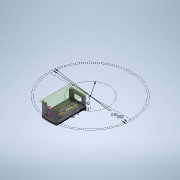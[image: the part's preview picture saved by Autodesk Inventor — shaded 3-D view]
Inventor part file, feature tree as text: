
AUTODESK INVENTOR PART (.ipt)
format: ipt  version: 2020 (Build 240168000, 168)  size: 668,160 bytes
history: native  units: mm
features: projected_geometry x30, extrude x16, sketch x11, fillet x10, other x6, chamfer x2
ambient origin geometry x8: Origin, YZ Plane, XZ Plane, XY Plane, X Axis, Y Axis, Z Axis, Center Point
bodies: Body1 (feature_tree)
feature tree (75):
  other  "Твердое тело1"
  sketch  "Эскиз1"
  extrude  "Выдавливание3"  Depth=202.0mm
  other  "РабПлоскость1"
  extrude  "Выдавливание1"  Depth=35.0mm
  other  "РабПлоскость2"
  sketch  "Эскиз2"
  extrude  "Выдавливание4"  Depth=68.0mm
  extrude  "Выдавливание5"  Depth=2.0mm
  sketch  "Эскиз4"
  extrude  "Выдавливание6"  Depth=2.0mm
  extrude  "Выдавливание7"  Depth=3.0mm
  other  "РабПлоскость3"
  extrude  "Выдавливание8"  Depth=3.0mm
  other  "РабПлоскость4"
  extrude  "Выдавливание9"  Depth=210.0mm
  sketch  "Эскиз8"
  extrude  "Выдавливание10"  Depth=20.0mm TaperAngle=0.0deg
  fillet  "Сопряжение1"  Radius=1.5mm
  fillet  "Сопряжение2"  Radius=28.0mm
  fillet  "Сопряжение3"  Radius=7.0mm
  fillet  "Сопряжение4"  Radius=20.0mm
  fillet  "Сопряжение5"  Radius=13.0mm
  extrude  "Выдавливание11"  Depth=5.0mm
  extrude  "Выдавливание12"  Depth=3.0mm
  fillet  "Сопряжение6"  Radius=10.0mm
  extrude  "Выдавливание13"  Depth=84.0mm
  chamfer  "Фаска1"  Distance=5.0mm
  fillet  "Сопряжение7"  Radius=52.0mm
  sketch  "Эскиз10"
  other  "РабПлоскость5"
  extrude  "Выдавливание14"  Depth=5.0mm TaperAngle=0.0deg
  fillet  "Сопряжение8"  Radius=35.0mm
  extrude  "Выдавливание15"  Depth=18.0mm
  fillet  "Сопряжение9"  Radius=3.0mm
  extrude  "Выдавливание16"  Depth=30.0mm TaperAngle=360.0deg
  fillet  "Сопряжение10"  Radius=0.5mm
  extrude  "Выдавливание17"  TaperAngle=0.0deg  [1 undecoded]
  chamfer  "Фаска2"  Distance=8.0mm
  projected_geometry  "Спроецированная петля1"
  projected_geometry  "Спроецированная петля7"
  projected_geometry  "Спроецированная петля8"
  sketch  "Эскиз3"
  projected_geometry  "Спроецированная петля9"
  projected_geometry  "Спроецированная петля10"
  projected_geometry  "Спроецированная петля11"
  projected_geometry  "Спроецированная петля12"
  sketch  "Эскиз5"
  projected_geometry  "Спроецированная петля13"
  projected_geometry  "Спроецированная петля14"
  projected_geometry  "Спроецированная петля15"
  projected_geometry  "Спроецированная петля16"
  projected_geometry  "Спроецированная петля17"
  sketch  "Эскиз6"
  projected_geometry  "Спроецированная петля18"
  projected_geometry  "Спроецированная петля19"
  projected_geometry  "Спроецированная петля20"
  projected_geometry  "Спроецированная петля21"
  projected_geometry  "Спроецированная петля22"
  projected_geometry  "Спроецированная петля23"
  projected_geometry  "Спроецированная петля24"
  projected_geometry  "Спроецированная петля25"
  projected_geometry  "Спроецированная петля26"
  projected_geometry  "Спроецированная петля27"
  projected_geometry  "Спроецированная петля28"
  sketch  "Эскиз9"
  projected_geometry  "Спроецированная петля29"
  projected_geometry  "Спроецированная петля30"
  sketch  "Эскиз11"
  projected_geometry  "Спроецированная петля31"
  projected_geometry  "Спроецированная петля32"
  projected_geometry  "Спроецированная петля33"
  sketch  "Эскиз12"
  projected_geometry  "Спроецированная петля34"
  projected_geometry  "Спроецированная петля35"
note: 1 required parameter value undecoded (feature->parameter linkage not recoverable at this tier; creation-order binding heuristic only, values carry confidence <= 0.55)
